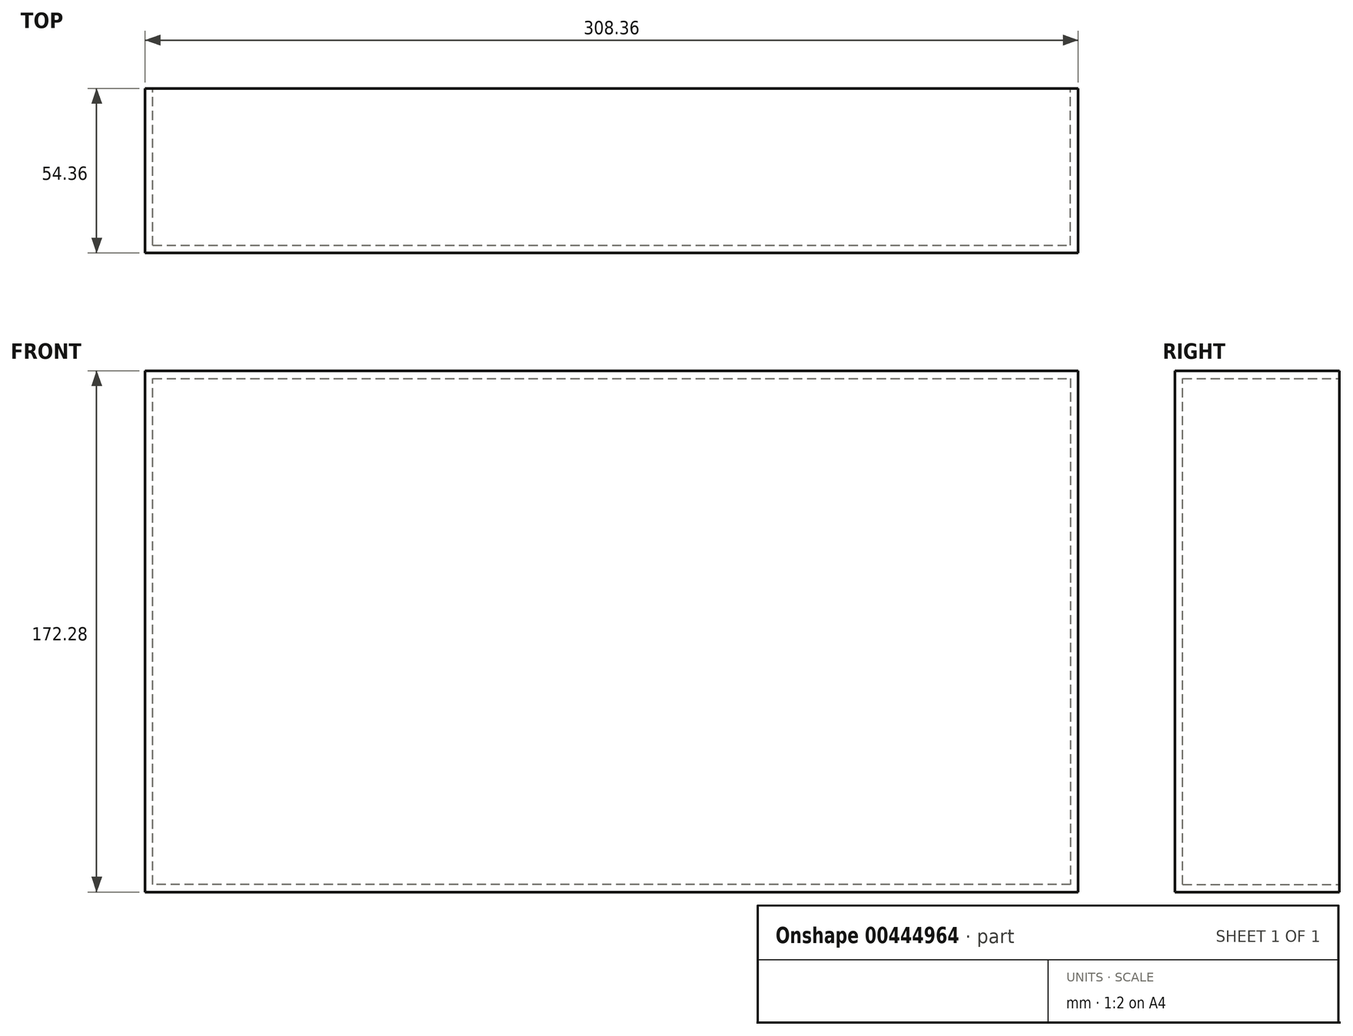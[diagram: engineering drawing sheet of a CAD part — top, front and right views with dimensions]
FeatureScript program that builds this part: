
annotation { "Feature Type Name" : "Feature", "Feature Type Description" : "" }
export const myFeature = defineFeature(function(context is Context, id is Id, definition is map)
    precondition{}
    {
        {
            var Q0;
            Q0=qCreatedBy(makeId("Front.planeOp"),FACE);
            var sketch = newSketch(context, id + "F0", { "sketchPlane" : qUnion([Q0])});
            skLineSegment(sketch, "E0", {"start": v(-154.2, 86.29) * mm, "end": v(154.16, 86.29) * mm});
            skLineSegment(sketch, "E1", {"start": v(154.16, 86.29) * mm, "end": v(154.16, -86) * mm});
            skLineSegment(sketch, "E2", {"start": v(154.16, -86) * mm, "end": v(-154.2, -86) * mm});
            skLineSegment(sketch, "E3", {"start": v(-154.2, -86) * mm, "end": v(-154.2, 86.29) * mm});
            skSolve(sketch);
        }
        {
            var Q0;
            Q0=makeQuery(id+"F0.imprint","IMPRINT",FACE,{"disambiguationData":[TD([[makeQuery(id+"F0.imprint","IMPRINT",EDGE,{"derivedFrom":sQuery(id+"F0.wireOp",EDGE,"E0")}),-1.0]])]});
            extrude(context, id + "F1", {"entities" : qUnion([Q0]), "depth" : 54.36 * mm});
        }
        {
            var Q0;
            Q0=makeQuery(id+"F1.opExtrude","CAP_FACE",FACE,{"disambiguationData":[OSD([sQuery(id+"F0.wireOp",EDGE,"E0"),sQuery(id+"F0.wireOp",EDGE,"E1"),sQuery(id+"F0.wireOp",EDGE,"E2"),sQuery(id+"F0.wireOp",EDGE,"E3")])],"isStart":true});
            shell(context, id + "F2", {"entities" : qUnion([Q0]), "thickness" : 2.54 * mm});
        }
        {
            var Q0;
            Q0=makeQuery(id+"F2.opShell","OFFSET_FACE",FACE,{"disambiguationData":[OSD([sQuery(id+"F0.wireOp",EDGE,"E0"),sQuery(id+"F0.wireOp",EDGE,"E1"),sQuery(id+"F0.wireOp",EDGE,"E2"),sQuery(id+"F0.wireOp",EDGE,"E3")])]});
            var sketch = newSketch(context, id + "F3", { "sketchPlane" : qUnion([Q0])});
            skSolve(sketch);
        }
        {
            var Q0;
            {var subQ0=sQuery(id+"F0.wireOp",EDGE,"E0");Q0=makeQuery(id+"F3.imprint","IMPRINT",FACE,{"disambiguationData":[TD([[makeQuery(id+"F3.imprint","IMPRINT",EDGE,{"derivedFrom":makeQuery(id+"F2.opShell","OFFSET_EDGE",EDGE,{"disambiguationData":[OSD([subQ0]),TDD([makeQuery(id+"F1.opExtrude","CAP_EDGE",EDGE,{"disambiguationData":[OSD([subQ0])],"isStart":false})])]})}),1.0]])]});}
            var sketch = newSketch(context, id + "F4", { "sketchPlane" : qUnion([Q0])});
            skLineSegment(sketch, "E4", {"start": v(-153.1, 0) * mm, "end": v(155.98, 0) * mm});
            skSolve(sketch);
        }
        {
            var Q0;
            Q0=sQuery(id+"F4.wireOp",EDGE,"E4");
            extrude(context, id + "F5", {"bodyType" : ToolBodyType.SURFACE, "surfaceEntities" : qUnion([Q0]), "depth" : 45.72 * mm});
        }
        {
            var Q0;
            {var subQ0=sQuery(id+"F0.wireOp",EDGE,"E0");Q0=makeQuery(id+"F3.imprint","IMPRINT",FACE,{"disambiguationData":[TD([[makeQuery(id+"F3.imprint","IMPRINT",EDGE,{"derivedFrom":makeQuery(id+"F2.opShell","OFFSET_EDGE",EDGE,{"disambiguationData":[OSD([subQ0]),TDD([makeQuery(id+"F1.opExtrude","CAP_EDGE",EDGE,{"disambiguationData":[OSD([subQ0])],"isStart":false})])]})}),1.0]])]});}
            var sketch = newSketch(context, id + "F6", { "sketchPlane" : qUnion([Q0])});
            skLineSegment(sketch, "E5", {"start": v(0, -82.88) * mm, "end": v(0, 86.25) * mm});
            skSolve(sketch);
        }
        {
            var Q0;
            Q0=sQuery(id+"F6.wireOp",EDGE,"E5");
            extrude(context, id + "F7", {"bodyType" : ToolBodyType.SURFACE, "surfaceEntities" : qUnion([Q0]), "depth" : 37.6 * mm});
        }
        {
            var Q0;
            {var subQ0=sQuery(id+"F0.wireOp",EDGE,"E0");Q0=makeQuery(id+"F3.imprint","IMPRINT",FACE,{"disambiguationData":[TD([[makeQuery(id+"F3.imprint","IMPRINT",EDGE,{"derivedFrom":makeQuery(id+"F2.opShell","OFFSET_EDGE",EDGE,{"disambiguationData":[OSD([subQ0]),TDD([makeQuery(id+"F1.opExtrude","CAP_EDGE",EDGE,{"disambiguationData":[OSD([subQ0])],"isStart":false})])]})}),1.0]])]});}
            var sketch = newSketch(context, id + "F8", { "sketchPlane" : qUnion([Q0])});
            skLineSegment(sketch, "E6", {"start": v(-73.81, 87.61) * mm, "end": v(-73.81, -82.9) * mm});
            skLineSegment(sketch, "E7", {"start": v(-73.81, -82.9) * mm, "end": v(-73.81, 87.61) * mm});
            skLineSegment(sketch, "E8", {"start": v(76.67, -83.23) * mm, "end": v(76.67, 87.61) * mm});
            skSolve(sketch);
        }
        {
            var Q0;
            Q0=sQuery(id+"F8.wireOp",EDGE,"E7");
            var Q1;
            Q1=sQuery(id+"F8.wireOp",EDGE,"E8");
            extrude(context, id + "F9", {"bodyType" : ToolBodyType.SURFACE, "surfaceEntities" : qUnion([Q0, Q1]), "depth" : 37.6 * mm});
        }
        {
            var Q0;
            {var subQ0=sQuery(id+"F0.wireOp",EDGE,"E0");Q0=makeQuery(id+"F3.imprint","IMPRINT",FACE,{"disambiguationData":[TD([[makeQuery(id+"F3.imprint","IMPRINT",EDGE,{"derivedFrom":makeQuery(id+"F2.opShell","OFFSET_EDGE",EDGE,{"disambiguationData":[OSD([subQ0]),TDD([makeQuery(id+"F1.opExtrude","CAP_EDGE",EDGE,{"disambiguationData":[OSD([subQ0])],"isStart":false})])]})}),1.0]])]});}
            var sketch = newSketch(context, id + "F10", { "sketchPlane" : qUnion([Q0])});
            skLineSegment(sketch, "E9", {"start": v(-74.9, 28.81) * mm, "end": v(-151.25, 28.81) * mm});
            skSolve(sketch);
        }
        {
            var Q0;
            Q0=sQuery(id+"F10.wireOp",EDGE,"E9");
            extrude(context, id + "F11", {"bodyType" : ToolBodyType.SURFACE, "surfaceEntities" : qUnion([Q0]), "depth" : 50.04 * mm});
        }
    });
